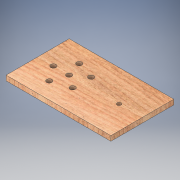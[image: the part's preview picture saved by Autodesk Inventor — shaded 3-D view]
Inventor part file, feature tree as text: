
AUTODESK INVENTOR PART (.ipt)
format: ipt  version: 2017 (Build 210142000, 142)  size: 140,288 bytes
history: native  units: in
note: dims shown in document units (in); Inventor stores cm internally (conversion verified against a paired STEP export)
features: extrude x2, sketch x2
ambient origin geometry x8: Origin, YZ Plane, XZ Plane, XY Plane, X Axis, Y Axis, Z Axis, Center Point
bodies: Solid1 (feature_tree)
feature tree (4):
  extrude  "Extrusion1"  Depth=9.9688in
  extrude  "Extrusion2"  Depth=0.4688in
  sketch  "Sketch1"  dims[d0=6.0in d1=9.9688in]
  sketch  "Sketch2"  dims[d2=2.2188in d3=0.375in d4=0.4688in d5=0.0in d6=0.5in d7=1.5in d8=0.5in d9=1.9685in d11=360.0deg d13=6.9688in d14=0.4688in d15=0.0in]
